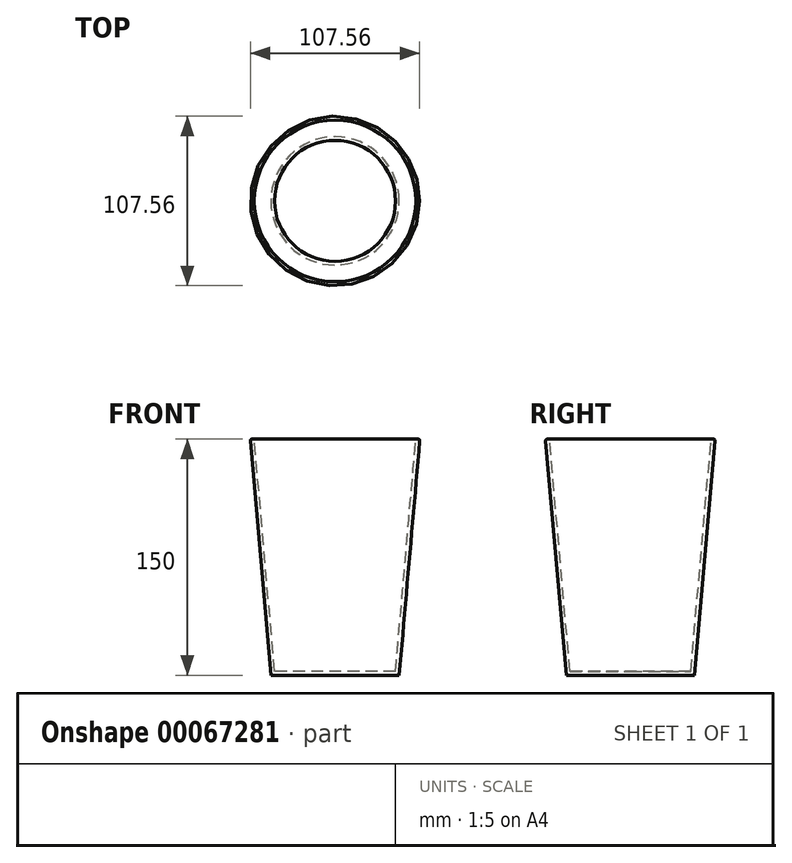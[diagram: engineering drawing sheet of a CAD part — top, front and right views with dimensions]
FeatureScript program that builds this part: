
annotation { "Feature Type Name" : "Feature", "Feature Type Description" : "" }
export const myFeature = defineFeature(function(context is Context, id is Id, definition is map)
    precondition{}
    {
        {
            var Q0;
            Q0=qCreatedBy(makeId("Top.planeOp"),FACE);
            var sketch = newSketch(context, id + "F0", { "sketchPlane" : qUnion([Q0])});
            skCircle(sketch, "E0", {"center": v(0, 0) * mm, "radius": 40.75 * mm});
            skSolve(sketch);
        }
        {
            var Q0;
            Q0=makeQuery(id+"F0.imprint","IMPRINT",FACE,{"disambiguationData":[TD([[makeQuery(id+"F0.imprint","IMPRINT",EDGE,{"derivedFrom":sQuery(id+"F0.wireOp",EDGE,"E0")}),1.0]])]});
            extrude(context, id + "F1", {"entities" : qUnion([Q0]), "depth" : 150 * mm, "hasDraft" : true, "draftAngle" : 5 * degree});
        }
        {
            var Q0;
            Q0=makeQuery(id+"F1.opExtrude","CAP_FACE",FACE,{"disambiguationData":[OSD([sQuery(id+"F0.wireOp",EDGE,"E0")])],"isStart":false});
            shell(context, id + "F2", {"entities" : qUnion([Q0]), "thickness" : 2.54 * mm});
        }
        {
            var Q0;
            Q0=makeQuery(id+"F1.opExtrude","CAP_EDGE",EDGE,{"disambiguationData":[OSD([sQuery(id+"F0.wireOp",EDGE,"E0")])],"isStart":false});
            fillet(context, id + "F3", {"entities" : qUnion([Q0]), "radius" : 1 * mm, "tangentPropagation" : true, "allowEdgeOverflow" : false});
        }
    });
